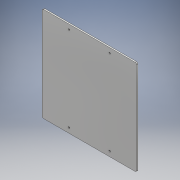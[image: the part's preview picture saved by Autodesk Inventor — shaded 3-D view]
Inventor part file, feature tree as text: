
AUTODESK INVENTOR PART (.ipt)
format: ipt  version: 2017 (Build 210142000, 142)  size: 110,592 bytes
history: native  units: mm
features: sketch x2, extrude x1, hole x1, fillet x1
ambient origin geometry x8: Origin, YZ Plane, XZ Plane, XY Plane, X Axis, Y Axis, Z Axis, Center Point
bodies: Solid1 (feature_tree)
feature tree (5):
  extrude  "Extrusion1"  Depth=3.0mm TaperAngle=0.0deg
  hole  "Hole1"  [1 undecoded]
  fillet  "Fillet1"  Radius=3.0mm
  sketch  "Sketch1"  dims[d0=210.0mm d1=3.0mm d2=0.0mm]
  sketch  "Sketch2"  dims[d3=188.25mm d4=90.5mm d5=3.5mm d6=6.0mm d7=7.0mm d8=2.0mm d9=90.0deg d10=8.0mm d11=20.594885mm d12=3.0mm]
note: 1 required parameter value undecoded (feature->parameter linkage not recoverable at this tier; creation-order binding heuristic only, values carry confidence <= 0.55)
